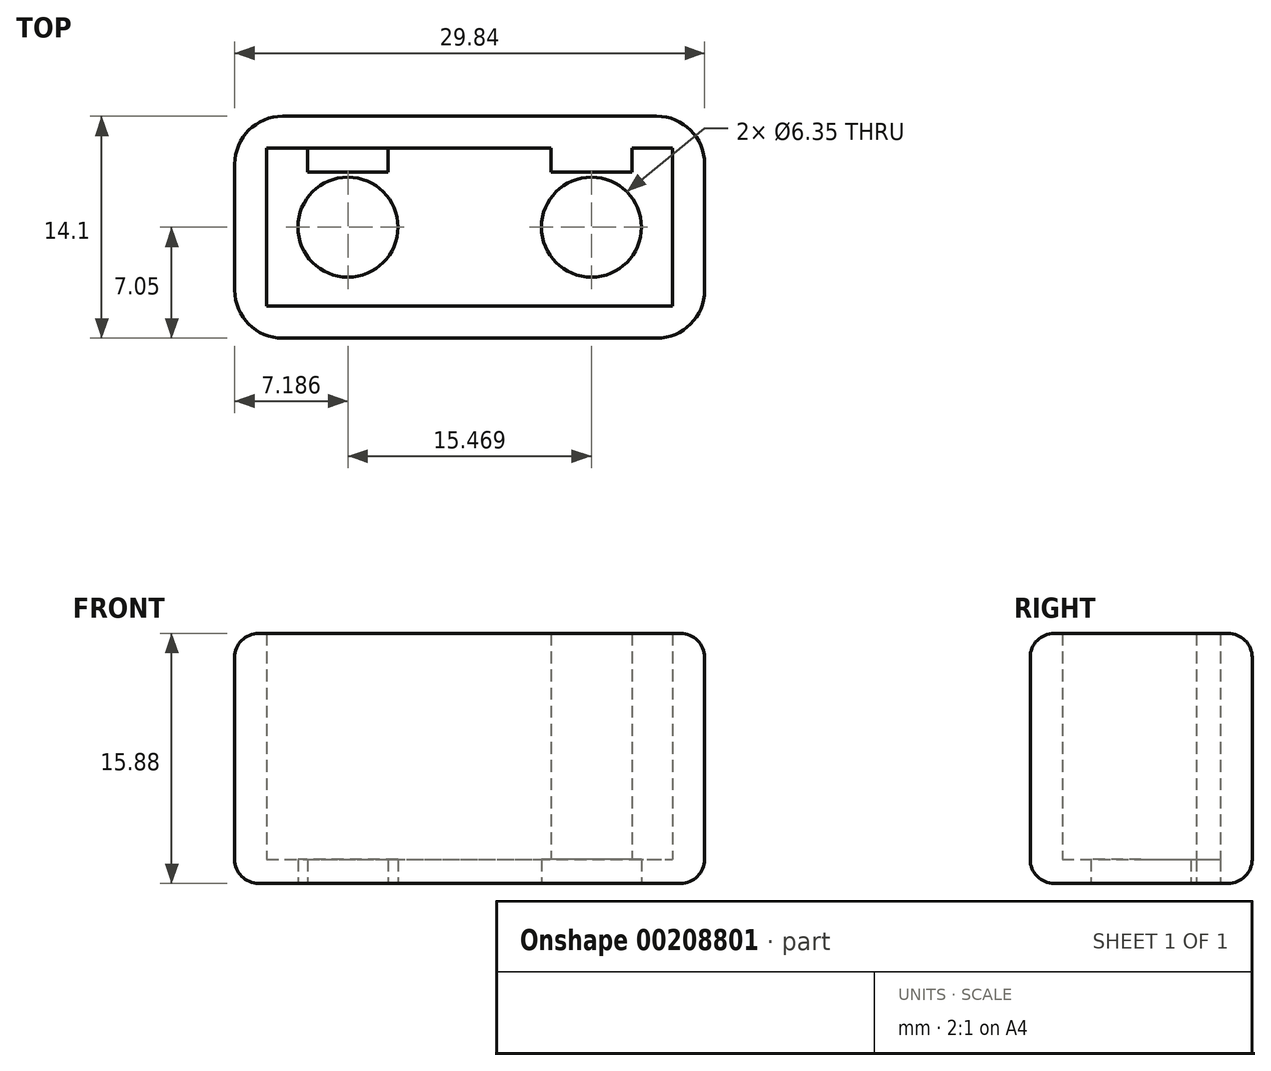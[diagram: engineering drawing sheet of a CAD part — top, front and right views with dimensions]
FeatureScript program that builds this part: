
annotation { "Feature Type Name" : "Feature", "Feature Type Description" : "" }
export const myFeature = defineFeature(function(context is Context, id is Id, definition is map)
    precondition{}
    {
        {
            var Q0;
            Q0=qCreatedBy(makeId("Top.planeOp"),FACE);
            var sketch = newSketch(context, id + "F0", { "sketchPlane" : qUnion([Q0])});
            skLineSegment(sketch, "E0.bottom", {"start": v(12.9, 5.02) * mm, "end": v(-12.9, 5.02) * mm});
            skLineSegment(sketch, "E0.top", {"start": v(12.9, -5.02) * mm, "end": v(-12.9, -5.02) * mm});
            skLineSegment(sketch, "E0.left", {"start": v(12.9, 5.02) * mm, "end": v(12.9, -5.02) * mm});
            skLineSegment(sketch, "E0.right", {"start": v(-12.9, 5.02) * mm, "end": v(-12.9, -5.02) * mm});
            skPoint(sketch, "E0.middle", {"position": v(0, 0) * mm});
            skLineSegment(sketch, "E1.0", {"start": v(14.92, 7.05) * mm, "end": v(-14.92, 7.05) * mm});
            skLineSegment(sketch, "E1.1", {"start": v(14.92, 7.05) * mm, "end": v(14.92, -7.05) * mm});
            skLineSegment(sketch, "E1.2", {"start": v(14.92, -7.05) * mm, "end": v(-14.92, -7.05) * mm});
            skLineSegment(sketch, "E1.3", {"start": v(-14.92, 7.05) * mm, "end": v(-14.92, -7.05) * mm});
            skPoint(sketch, "E2", {"position": v(-7.73, 0) * mm});
            skPoint(sketch, "E2.positionSnap0", {"position": v(-12.9, 0) * mm});
            skLineSegment(sketch, "E3", {"start": v(0, 5.02) * mm, "end": v(0, -5.02) * mm, "construction": true});
            skPoint(sketch, "E4.MirrorP", {"position": v(7.73, 0) * mm});
            skLineSegment(sketch, "E5", {"start": v(-12.9, 3.5) * mm, "end": v(12.9, 3.5) * mm});
            skLineSegment(sketch, "E6", {"start": v(-7.73, 3.5) * mm, "end": v(-7.73, 5.02) * mm, "construction": true});
            skLineSegment(sketch, "E7", {"start": v(-7.73, 3.5) * mm, "end": v(-10.3, 3.5) * mm});
            skLineSegment(sketch, "E8", {"start": v(-10.3, 3.5) * mm, "end": v(-10.3, 5.02) * mm});
            skLineSegment(sketch, "E9.MirrorCS", {"start": v(-5.17, 3.5) * mm, "end": v(-5.17, 5.02) * mm});
            skLineSegment(sketch, "E10.MirrorCS", {"start": v(5.17, 3.5) * mm, "end": v(5.17, 5.02) * mm});
            skLineSegment(sketch, "E11.MirrorCS", {"start": v(10.3, 3.5) * mm, "end": v(10.3, 5.02) * mm});
            skLineSegment(sketch, "E12.MirrorCS", {"start": v(7.73, 3.5) * mm, "end": v(10.3, 3.5) * mm});
            skLineSegment(sketch, "E13.MirrorCS", {"start": v(7.73, 3.5) * mm, "end": v(7.73, 5.02) * mm, "construction": true});
            skSolve(sketch);
        }
        {
            var Q0;
            Q0=makeQuery(id+"F0.imprint","IMPRINT",FACE,{"disambiguationData":[TD([[makeQuery(id+"F0.imprint","IMPRINT",EDGE,{"derivedFrom":sQuery(id+"F0.wireOp",EDGE,"E0.bottom")}),-1.0]])]});
            var Q1;
            {var subQ0=sQuery(id+"F0.wireOp",EDGE,"E0.top");Q1=makeQuery(id+"F0.imprint","IMPRINT",FACE,{"disambiguationData":[TD([[makeQuery(id+"F0.imprint","IMPRINT",EDGE,{"derivedFrom":subQ0}),-1.0]])]});}
            var Q2;
            {var subQ0=sQuery(id+"F0.wireOp",EDGE,"E0.bottom");Q2=makeQuery(id+"F0.imprint","IMPRINT",FACE,{"disambiguationData":[TD([[makeQuery(id+"F0.imprint","IMPRINT",EDGE,{"derivedFrom":subQ0}),1.0]])]});}
            var Q3;
            {var subQ1=sQuery(id+"F0.wireOp",EDGE,"E7");Q3=makeQuery(id+"F0.imprint","IMPRINT",FACE,{"disambiguationData":[TD([[makeQuery(id+"F0.imprint","IMPRINT",EDGE,{"derivedFrom":subQ1}),-1.0]])]});}
            var Q4;
            {var subQ0=sQuery(id+"F0.wireOp",EDGE,"E10.MirrorCS");Q4=makeQuery(id+"F0.imprint","IMPRINT",FACE,{"disambiguationData":[TD([[makeQuery(id+"F0.imprint","IMPRINT",EDGE,{"derivedFrom":subQ0}),-1.0]])]});}
            extrude(context, id + "F1", {"entities" : qUnion([Q0, Q1, Q2, Q3, Q4]), "depth" : 1.52 * mm});
        }
        {
            var Q0;
            Q0=makeQuery(id+"F0.imprint","IMPRINT",FACE,{"disambiguationData":[TD([[makeQuery(id+"F0.imprint","IMPRINT",EDGE,{"derivedFrom":sQuery(id+"F0.wireOp",EDGE,"E0.bottom")}),-1.0]])]});
            var Q1;
            {var subQ1=sQuery(id+"F0.wireOp",EDGE,"E7");Q1=makeQuery(id+"F0.imprint","IMPRINT",FACE,{"disambiguationData":[TD([[makeQuery(id+"F0.imprint","IMPRINT",EDGE,{"derivedFrom":subQ1}),-1.0]])]});}
            var Q2;
            {var subQ0=sQuery(id+"F0.wireOp",EDGE,"E10.MirrorCS");Q2=makeQuery(id+"F0.imprint","IMPRINT",FACE,{"disambiguationData":[TD([[makeQuery(id+"F0.imprint","IMPRINT",EDGE,{"derivedFrom":subQ0}),-1.0]])]});}
            extrude(context, id + "F2", {"entities" : qUnion([Q0, Q1, Q2]), "operationType" : NewBodyOperationType.ADD, "depth" : 15.88 * mm});
        }
        {
            var Q0;
            Q0=sQuery(id+"F0.wireOp",VERTEX,"E2");
            var Q1;
            Q1=sQuery(id+"F0.wireOp",VERTEX,"E4.MirrorP");
            var Q2;
            Q2=makeQuery(id+"F1.opExtrude","SWEPT_BODY",BODY,{"disambiguationData":[OSD([sQuery(id+"F0.wireOp",EDGE,"E1.0"),sQuery(id+"F0.wireOp",EDGE,"E1.1"),sQuery(id+"F0.wireOp",EDGE,"E1.2"),sQuery(id+"F0.wireOp",EDGE,"E1.3")])]});
            hole(context, id + "F3", {"style" : HoleStyle.SIMPLE, "endStyle" : HoleEndStyle.BLIND, "oppositeDirection" : true, "holeDiameter" : 6.35 * mm, "holeDepth" : 6.73 * mm, "locations" : qUnion([Q0, Q1]), "scope" : qUnion([Q2])});
        }
        {
            var Q0;
            {var subQ0=sQuery(id+"F0.wireOp",EDGE,"E1.3");var subQ1=sQuery(id+"F0.wireOp",EDGE,"E1.0");Q0=makeQuery(id+"F2.boolean.opBoolean","MERGE",EDGE,{"derivedFrom":[makeQuery(id+"F1.opExtrude","SWEPT_EDGE",EDGE,{"disambiguationData":[OSD([subQ1,subQ0])]}),makeQuery(id+"F2.opExtrude","SWEPT_EDGE",EDGE,{"disambiguationData":[OSD([subQ1,subQ0])]})]});}
            var Q1;
            {var subQ0=sQuery(id+"F0.wireOp",EDGE,"E1.3");var subQ1=sQuery(id+"F0.wireOp",EDGE,"E1.2");Q1=makeQuery(id+"F2.boolean.opBoolean","MERGE",EDGE,{"derivedFrom":[makeQuery(id+"F1.opExtrude","SWEPT_EDGE",EDGE,{"disambiguationData":[OSD([subQ1,subQ0])]}),makeQuery(id+"F2.opExtrude","SWEPT_EDGE",EDGE,{"disambiguationData":[OSD([subQ1,subQ0])]})]});}
            var Q2;
            {var subQ0=sQuery(id+"F0.wireOp",EDGE,"E1.2");var subQ1=sQuery(id+"F0.wireOp",EDGE,"E1.1");Q2=makeQuery(id+"F2.boolean.opBoolean","MERGE",EDGE,{"derivedFrom":[makeQuery(id+"F1.opExtrude","SWEPT_EDGE",EDGE,{"disambiguationData":[OSD([subQ1,subQ0])]}),makeQuery(id+"F2.opExtrude","SWEPT_EDGE",EDGE,{"disambiguationData":[OSD([subQ1,subQ0])]})]});}
            var Q3;
            {var subQ0=sQuery(id+"F0.wireOp",EDGE,"E1.1");var subQ1=sQuery(id+"F0.wireOp",EDGE,"E1.0");Q3=makeQuery(id+"F2.boolean.opBoolean","MERGE",EDGE,{"derivedFrom":[makeQuery(id+"F1.opExtrude","SWEPT_EDGE",EDGE,{"disambiguationData":[OSD([subQ1,subQ0])]}),makeQuery(id+"F2.opExtrude","SWEPT_EDGE",EDGE,{"disambiguationData":[OSD([subQ1,subQ0])]})]});}
            fillet(context, id + "F4", {"entities" : qUnion([Q0, Q1, Q2, Q3]), "radius" : 3.05 * mm, "tangentPropagation" : true, "allowEdgeOverflow" : false});
        }
        {
            var Q0;
            Q0=makeQuery(id+"F2.opExtrude","CAP_EDGE",EDGE,{"disambiguationData":[OSD([sQuery(id+"F0.wireOp",EDGE,"E1.2")])],"isStart":false});
            var Q1;
            Q1=makeQuery(id+"F1.opExtrude","CAP_EDGE",EDGE,{"disambiguationData":[OSD([sQuery(id+"F0.wireOp",EDGE,"E1.0")])],"isStart":true});
            fillet(context, id + "F5", {"entities" : qUnion([Q0, Q1]), "radius" : 1.52 * mm, "tangentPropagation" : true, "allowEdgeOverflow" : false});
        }
    });
